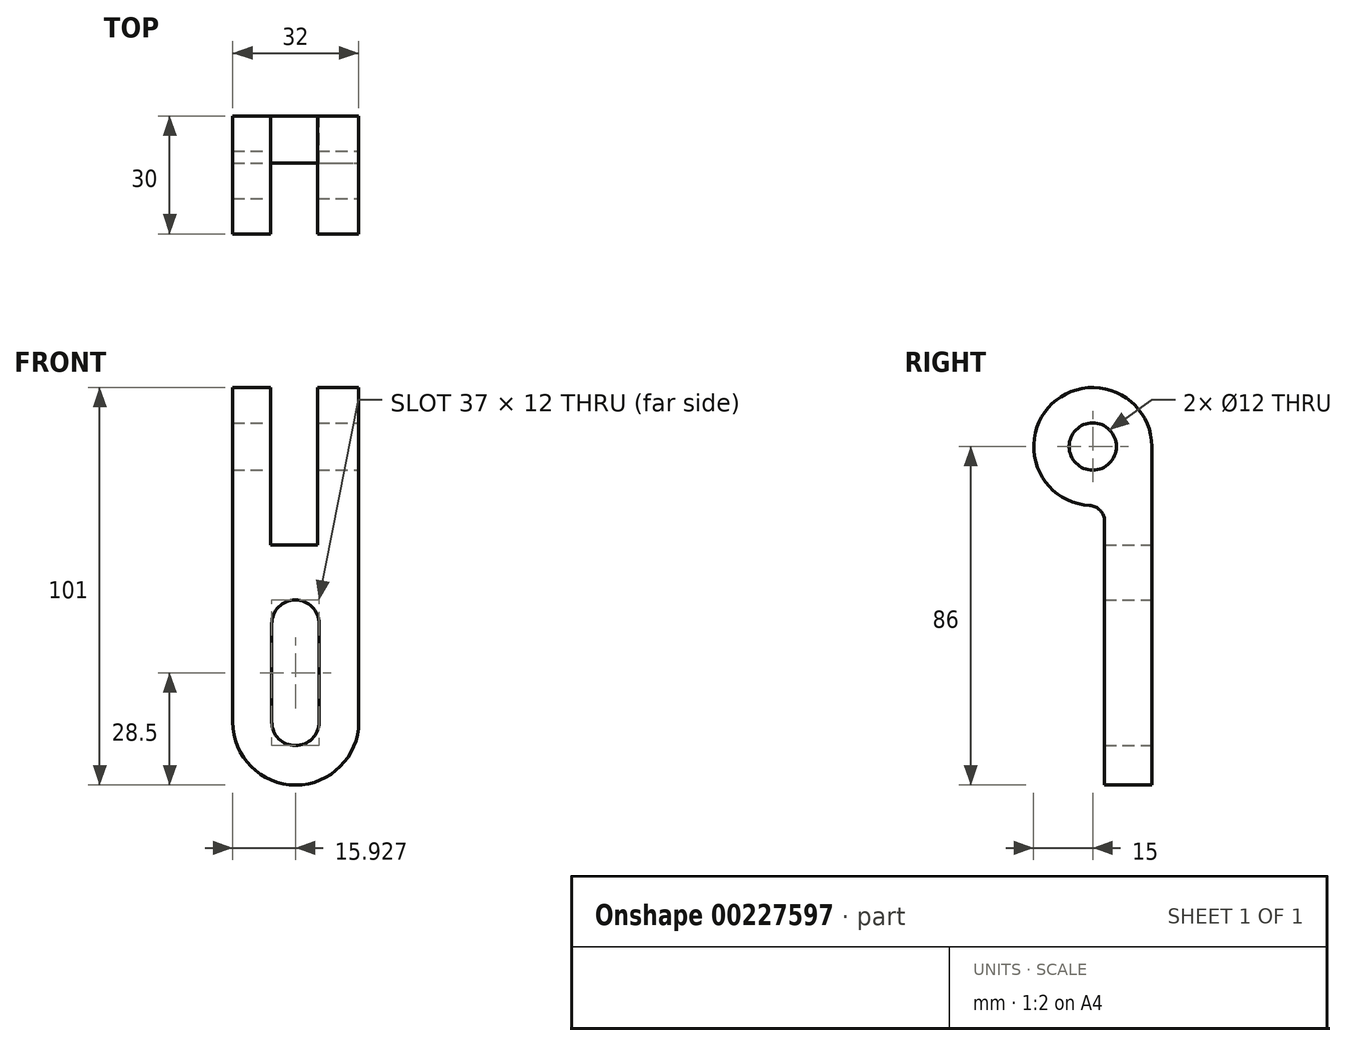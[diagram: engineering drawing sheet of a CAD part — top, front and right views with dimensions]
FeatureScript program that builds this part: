
annotation { "Feature Type Name" : "Feature", "Feature Type Description" : "" }
export const myFeature = defineFeature(function(context is Context, id is Id, definition is map)
    precondition{}
    {
        {
            var Q0;
            Q0=qCreatedBy(makeId("Front.planeOp"),FACE);
            var sketch = newSketch(context, id + "F0", { "sketchPlane" : qUnion([Q0])});
            skLineSegment(sketch, "E0", {"start": v(0, 19.8) * mm, "end": v(0, 104.8) * mm});
            skLineSegment(sketch, "E1", {"start": v(0, 104.8) * mm, "end": v(9.6, 104.8) * mm});
            skLineSegment(sketch, "E2", {"start": v(9.6, 104.8) * mm, "end": v(9.6, 64.8) * mm});
            skLineSegment(sketch, "E3", {"start": v(9.6, 64.8) * mm, "end": v(21.6, 64.8) * mm});
            skLineSegment(sketch, "E4", {"start": v(21.6, 64.8) * mm, "end": v(21.6, 104.8) * mm});
            skLineSegment(sketch, "E5", {"start": v(21.6, 104.8) * mm, "end": v(32, 104.8) * mm});
            skLineSegment(sketch, "E6", {"start": v(32, 104.8) * mm, "end": v(32, 19.8) * mm});
            skArc(sketch, "E7", {"start": v(0, 19.8) * mm, "mid": v(16, 3.8) * mm, "end": v(32, 19.8) * mm});
            skLineSegment(sketch, "E8", {"start": v(-25.92, 19.8) * mm, "end": v(51.64, 19.8) * mm, "construction": true});
            skLineSegment(sketch, "E9", {"start": v(16, 44.8) * mm, "end": v(16, -17.35) * mm, "construction": true});
            skLineSegment(sketch, "E10", {"start": v(9.93, 44.8) * mm, "end": v(9.93, 19.8) * mm});
            skLineSegment(sketch, "E11", {"start": v(9.93, 19.8) * mm, "end": v(21.93, 19.8) * mm});
            skLineSegment(sketch, "E12", {"start": v(21.93, 19.8) * mm, "end": v(21.93, 44.8) * mm});
            skArc(sketch, "E13", {"start": v(21.93, 44.8) * mm, "mid": v(15.93, 50.8) * mm, "end": v(9.93, 44.8) * mm});
            skArc(sketch, "E14", {"start": v(9.93, 19.8) * mm, "mid": v(15.93, 13.8) * mm, "end": v(21.93, 19.8) * mm});
            skLineSegment(sketch, "E15", {"start": v(4.4, 44.8) * mm, "end": v(38.46, 44.8) * mm, "construction": true});
            skLineSegment(sketch, "E16", {"start": v(-19.51, 89.8) * mm, "end": v(55, 89.8) * mm, "construction": true});
            skLineSegment(sketch, "E17", {"start": v(0, 95.8) * mm, "end": v(9.6, 95.8) * mm, "construction": true});
            skLineSegment(sketch, "E18", {"start": v(0, 83.8) * mm, "end": v(9.6, 83.8) * mm, "construction": true});
            skLineSegment(sketch, "E19", {"start": v(9.6, 104.8) * mm, "end": v(21.6, 104.8) * mm});
            skSolve(sketch);
        }
        {
            var Q0;
            Q0 = qSketchRegion(id + "F0", true);
            extrude(context, id + "F1", {"entities" : qUnion([Q0]), "depth" : 12 * mm});
        }
        {
            var Q0;
            Q0=makeQuery(id+"F1.opExtrude","SWEPT_FACE",FACE,{"disambiguationData":[OSD([sQuery(id+"F0.wireOp",EDGE,"E6")])]});
            var sketch = newSketch(context, id + "F2", { "sketchPlane" : qUnion([Q0])});
            skLineSegment(sketch, "E20.0.0", {"start": v(0, 19.8) * mm, "end": v(0, 104.8) * mm, "construction": true});
            skLineSegment(sketch, "E20.0.1", {"start": v(0, 104.8) * mm, "end": v(-12, 104.8) * mm, "construction": true});
            skLineSegment(sketch, "E20.0.2", {"start": v(-12, 70.83) * mm, "end": v(-12, 19.8) * mm, "construction": true});
            skLineSegment(sketch, "E20.0.3", {"start": v(-12, 19.8) * mm, "end": v(0, 19.8) * mm, "construction": true});
            skPoint(sketch, "E21.0", {"position": v(0, 89.8) * mm});
            skLineSegment(sketch, "E22", {"start": v(0, 89.8) * mm, "end": v(-44.5, 89.8) * mm, "construction": true});
            skLineSegment(sketch, "E23", {"start": v(-15, 116.67) * mm, "end": v(-15, 62.6) * mm, "construction": true});
            skArc(sketch, "E24", {"start": v(0, 89.8) * mm, "mid": v(-25.32, 100.68) * mm, "end": v(-15.79, 74.82) * mm});
            skCircle(sketch, "E25", {"center": v(-15, 89.8) * mm, "radius": 6 * mm});
            skLineSegment(sketch, "E26", {"start": v(-12, 75.1) * mm, "end": v(-12, 39.19) * mm});
            skArc(sketch, "E27.filletArc", {"start": v(-12, 70.83) * mm, "mid": v(-13.1, 73.58) * mm, "end": v(-15.79, 74.82) * mm});
            skSolve(sketch);
        }
        {
            var Q0;
            {var subQ0=sQuery(id+"F2.wireOp",EDGE,"E27.filletArc");Q0=makeQuery(id+"F2.imprint","IMPRINT",FACE,{"disambiguationData":[TD([[makeQuery(id+"F2.imprint","IMPRINT",EDGE,{"derivedFrom":subQ0}),-1.0]])]});}
            extrude(context, id + "F3", {"entities" : qUnion([Q0]), "operationType" : NewBodyOperationType.ADD, "oppositeDirection" : true, "depth" : 32 * mm});
        }
        {
            var Q0;
            {var subQ0=sQuery(id+"F2.wireOp",EDGE,"E25");var subQ1=makeQuery(id+"F1.opExtrude","CAP_EDGE",EDGE,{"disambiguationData":[OSD([sQuery(id+"F0.wireOp",EDGE,"E6")])],"isStart":false});var subQ2=makeQuery(id+"F2.imprint","INTERSECT",VERTEX,{"disambiguationData":[OD(0.0)],"derivedFrom":[subQ1,subQ0]});Q0=makeQuery(id+"F2.imprint","IMPRINT",FACE,{"disambiguationData":[TD([[makeQuery(id+"F2.imprint","IMPRINT",EDGE,{"disambiguationData":[TD([[subQ2,-1.0]])],"derivedFrom":subQ0}),1.0]])]});}
            extrude(context, id + "F4", {"entities" : qUnion([Q0]), "operationType" : NewBodyOperationType.REMOVE, "endBound" : BoundingType.THROUGH_ALL, "oppositeDirection" : true, "depth" : 25 * mm});
        }
        {
            var Q0;
            {var subQ1=sQuery(id+"F0.wireOp",EDGE,"E6");var subQ6=makeQuery(id+"F1.opExtrude","SWEPT_EDGE",EDGE,{"disambiguationData":[OSD([sQuery(id+"F0.wireOp",EDGE,"E5"),subQ1])]});Q0=makeQuery(id+"F2.imprint","IMPRINT",FACE,{"disambiguationData":[TD([[makeQuery(id+"F2.imprint","IMPRINT",EDGE,{"derivedFrom":subQ6}),-1.0]])]});}
            extrude(context, id + "F5", {"entities" : qUnion([Q0]), "operationType" : NewBodyOperationType.REMOVE, "endBound" : BoundingType.THROUGH_ALL, "oppositeDirection" : true, "depth" : 25 * mm});
        }
        {
            var Q0;
            Q0=makeQuery(id+"F0.imprint","IMPRINT",FACE,{"disambiguationData":[TD([[makeQuery(id+"F0.imprint","IMPRINT",EDGE,{"derivedFrom":sQuery(id+"F0.wireOp",EDGE,"E2")}),1.0]])]});
            extrude(context, id + "F6", {"entities" : qUnion([Q0]), "operationType" : NewBodyOperationType.REMOVE, "endBound" : BoundingType.THROUGH_ALL, "depth" : 25 * mm});
        }
    });
